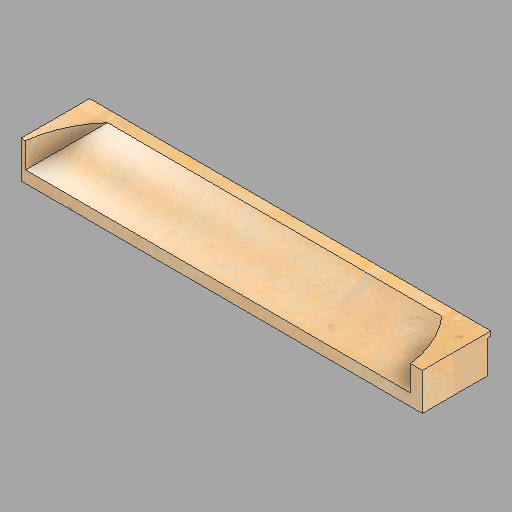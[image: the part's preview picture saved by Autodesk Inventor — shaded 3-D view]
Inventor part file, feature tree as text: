
AUTODESK INVENTOR PART (.ipt)
format: ipt  version: 2022.2 (Build 262287010, 287A)  size: 235,520 bytes
history: native  units: in
note: dims shown in document units (in); Inventor stores cm internally (conversion verified against a paired STEP export)
features: revolve x2, direct_edit x1, other x1
ambient origin geometry x8: Origin, YZ Plane, XZ Plane, XY Plane, X Axis, Y Axis, Z Axis, Center Point
bodies: Solid1 (feature_tree)
feature tree (4):
  direct_edit  "Direct Edit1"
  other  "Head (L)"
  revolve  "Rotate1"  [1 undecoded]
  revolve  "Rotate2"  [1 undecoded]
note: 2 required parameter values undecoded (feature->parameter linkage not recoverable at this tier; creation-order binding heuristic only, values carry confidence <= 0.55)
